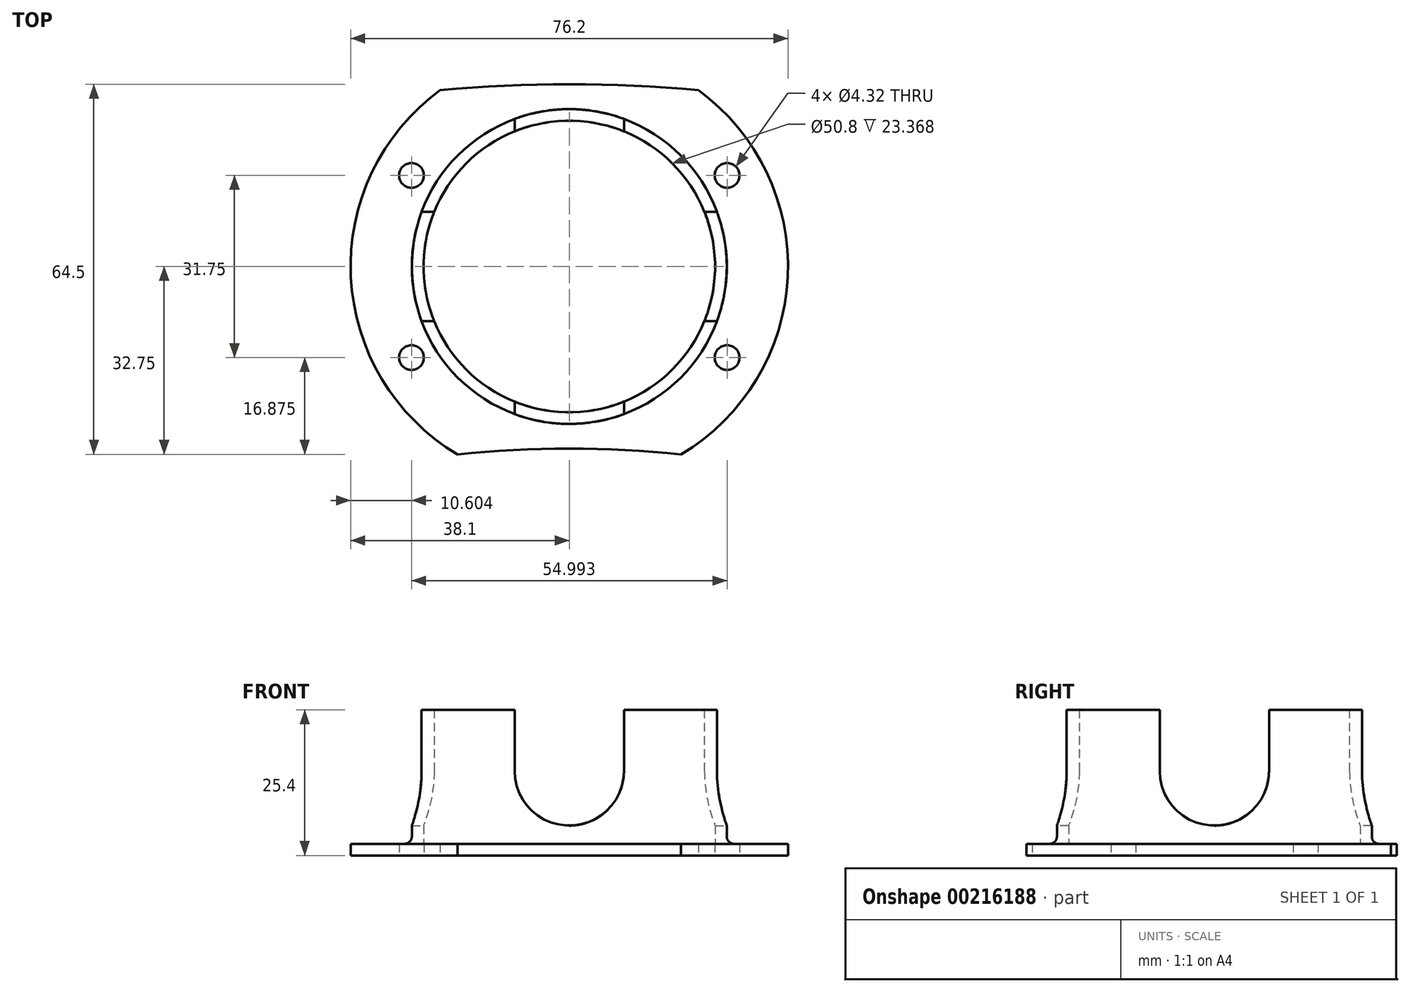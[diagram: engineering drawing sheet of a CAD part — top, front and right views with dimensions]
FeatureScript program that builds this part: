
annotation { "Feature Type Name" : "Feature", "Feature Type Description" : "" }
export const myFeature = defineFeature(function(context is Context, id is Id, definition is map)
    precondition{}
    {
        {
            var Q0;
            Q0=qCreatedBy(makeId("Top.planeOp"),FACE);
            var sketch = newSketch(context, id + "F0", { "sketchPlane" : qUnion([Q0])});
            skCircle(sketch, "E0", {"center": v(0, 0) * mm, "radius": 190.5 * mm});
            skCircle(sketch, "E1", {"center": v(0, 0) * mm, "radius": 254 * mm});
            skLineSegment(sketch, "E2", {"start": v(0, 0) * mm, "end": v(0, 254) * mm});
            skLineSegment(sketch, "E3.1.0", {"start": v(0, 0) * mm, "end": v(-254, 0) * mm});
            skLineSegment(sketch, "E3.2.0", {"start": v(0, 0) * mm, "end": v(0, -254) * mm});
            skLineSegment(sketch, "E3.3.0", {"start": v(0, 0) * mm, "end": v(254, 0) * mm});
            skLineSegment(sketch, "E4", {"start": v(0, 254) * mm, "end": v(0, 190.5) * mm});
            skCircle(sketch, "E5", {"center": v(0, 222.25) * mm, "radius": 31.75 * mm});
            skCircle(sketch, "E6", {"center": v(0, 222.25) * mm, "radius": 25.4 * mm});
            skCircle(sketch, "E7", {"center": v(0, 222.25) * mm, "radius": 38.1 * mm});
            skLineSegment(sketch, "E8", {"start": v(0, 222.25) * mm, "end": v(0, 254) * mm});
            skLineSegment(sketch, "E9.1.0", {"start": v(0, 222.25) * mm, "end": v(-27.5, 238.12) * mm});
            skLineSegment(sketch, "E9.2.0", {"start": v(0, 222.25) * mm, "end": v(-27.5, 206.38) * mm});
            skLineSegment(sketch, "E9.3.0", {"start": v(0, 222.25) * mm, "end": v(0, 190.5) * mm});
            skLineSegment(sketch, "E9.4.0", {"start": v(0, 222.25) * mm, "end": v(27.5, 206.37) * mm});
            skLineSegment(sketch, "E9.5.0", {"start": v(0, 222.25) * mm, "end": v(27.5, 238.12) * mm});
            skCircle(sketch, "E10", {"center": v(0, 222.25) * mm, "radius": 27.43 * mm});
            skSolve(sketch);
        }
        {
            var Q0;
            {var subQ0=sQuery(id+"F0.wireOp",EDGE,"E5");var subQ1=makeQuery(id+"F0.imprint","INTERSECT",VERTEX,{"derivedFrom":[subQ0,sQuery(id+"F0.wireOp",EDGE,"E9.1.0")]});Q0=makeQuery(id+"F0.imprint","IMPRINT",FACE,{"disambiguationData":[TD([[makeQuery(id+"F0.imprint","IMPRINT",EDGE,{"disambiguationData":[TD([[subQ1,-1.0]])],"derivedFrom":subQ0}),-1.0]])]});}
            var Q1;
            {var subQ1=sQuery(id+"F0.wireOp",EDGE,"E5");var subQ3=sQuery(id+"F0.wireOp",EDGE,"E9.1.0");var subQ4=makeQuery(id+"F0.imprint","INTERSECT",VERTEX,{"derivedFrom":[subQ1,subQ3]});Q1=makeQuery(id+"F0.imprint","IMPRINT",FACE,{"disambiguationData":[TD([[makeQuery(id+"F0.imprint","IMPRINT",EDGE,{"disambiguationData":[TD([[subQ4,1.0]])],"derivedFrom":subQ3}),-1.0]])]});}
            var Q2;
            {var subQ0=sQuery(id+"F0.wireOp",EDGE,"E9.1.0");var subQ1=sQuery(id+"F0.wireOp",EDGE,"E5");var subQ2=makeQuery(id+"F0.imprint","INTERSECT",VERTEX,{"derivedFrom":[subQ1,subQ0]});Q2=makeQuery(id+"F0.imprint","IMPRINT",FACE,{"disambiguationData":[TD([[makeQuery(id+"F0.imprint","IMPRINT",EDGE,{"disambiguationData":[TD([[subQ2,-1.0]])],"derivedFrom":subQ1}),1.0]])]});}
            var Q3;
            {var subQ0=sQuery(id+"F0.wireOp",EDGE,"E9.1.0");var subQ1=sQuery(id+"F0.wireOp",EDGE,"E6");var subQ2=makeQuery(id+"F0.imprint","INTERSECT",VERTEX,{"derivedFrom":[subQ1,subQ0]});Q3=makeQuery(id+"F0.imprint","IMPRINT",FACE,{"disambiguationData":[TD([[makeQuery(id+"F0.imprint","IMPRINT",EDGE,{"disambiguationData":[TD([[subQ2,-1.0]])],"derivedFrom":subQ1}),-1.0]])]});}
            var Q4;
            {var subQ1=sQuery(id+"F0.wireOp",EDGE,"E5");var subQ3=sQuery(id+"F0.wireOp",EDGE,"E9.2.0");var subQ4=makeQuery(id+"F0.imprint","INTERSECT",VERTEX,{"derivedFrom":[subQ1,subQ3]});Q4=makeQuery(id+"F0.imprint","IMPRINT",FACE,{"disambiguationData":[TD([[makeQuery(id+"F0.imprint","IMPRINT",EDGE,{"disambiguationData":[TD([[subQ4,1.0]])],"derivedFrom":subQ3}),1.0]])]});}
            var Q5;
            {var subQ0=sQuery(id+"F0.wireOp",EDGE,"E9.2.0");var subQ1=sQuery(id+"F0.wireOp",EDGE,"E6");var subQ2=makeQuery(id+"F0.imprint","INTERSECT",VERTEX,{"derivedFrom":[subQ1,subQ0]});Q5=makeQuery(id+"F0.imprint","IMPRINT",FACE,{"disambiguationData":[TD([[makeQuery(id+"F0.imprint","IMPRINT",EDGE,{"disambiguationData":[TD([[subQ2,-1.0]])],"derivedFrom":subQ1}),-1.0]])]});}
            var Q6;
            {var subQ0=sQuery(id+"F0.wireOp",EDGE,"E9.2.0");var subQ1=sQuery(id+"F0.wireOp",EDGE,"E6");var subQ2=makeQuery(id+"F0.imprint","INTERSECT",VERTEX,{"derivedFrom":[subQ1,subQ0]});Q6=makeQuery(id+"F0.imprint","IMPRINT",FACE,{"disambiguationData":[TD([[makeQuery(id+"F0.imprint","IMPRINT",EDGE,{"disambiguationData":[TD([[subQ2,-1.0]])],"derivedFrom":subQ1}),1.0]])]});}
            var Q7;
            {var subQ0=sQuery(id+"F0.wireOp",EDGE,"E9.1.0");var subQ1=sQuery(id+"F0.wireOp",EDGE,"E6");var subQ2=makeQuery(id+"F0.imprint","INTERSECT",VERTEX,{"derivedFrom":[subQ1,subQ0]});Q7=makeQuery(id+"F0.imprint","IMPRINT",FACE,{"disambiguationData":[TD([[makeQuery(id+"F0.imprint","IMPRINT",EDGE,{"disambiguationData":[TD([[subQ2,-1.0]])],"derivedFrom":subQ1}),1.0]])]});}
            var Q8;
            {var subQ0=sQuery(id+"F0.wireOp",EDGE,"E8");var subQ1=sQuery(id+"F0.wireOp",EDGE,"E6");var subQ2=makeQuery(id+"F0.imprint","INTERSECT",VERTEX,{"derivedFrom":[subQ1,subQ0]});Q8=makeQuery(id+"F0.imprint","IMPRINT",FACE,{"disambiguationData":[TD([[makeQuery(id+"F0.imprint","IMPRINT",EDGE,{"disambiguationData":[TD([[subQ2,-1.0]])],"derivedFrom":subQ1}),1.0]])]});}
            var Q9;
            {var subQ0=sQuery(id+"F0.wireOp",EDGE,"E8");var subQ1=sQuery(id+"F0.wireOp",EDGE,"E6");var subQ2=makeQuery(id+"F0.imprint","INTERSECT",VERTEX,{"derivedFrom":[subQ1,subQ0]});Q9=makeQuery(id+"F0.imprint","IMPRINT",FACE,{"disambiguationData":[TD([[makeQuery(id+"F0.imprint","IMPRINT",EDGE,{"disambiguationData":[TD([[subQ2,-1.0]])],"derivedFrom":subQ1}),-1.0]])]});}
            var Q10;
            {var subQ1=sQuery(id+"F0.wireOp",EDGE,"E5");var subQ3=sQuery(id+"F0.wireOp",EDGE,"E9.5.0");var subQ4=makeQuery(id+"F0.imprint","INTERSECT",VERTEX,{"derivedFrom":[subQ1,subQ3]});Q10=makeQuery(id+"F0.imprint","IMPRINT",FACE,{"disambiguationData":[TD([[makeQuery(id+"F0.imprint","IMPRINT",EDGE,{"disambiguationData":[TD([[subQ4,1.0]])],"derivedFrom":subQ3}),1.0]])]});}
            var Q11;
            {var subQ0=sQuery(id+"F0.wireOp",EDGE,"E8");var subQ1=sQuery(id+"F0.wireOp",EDGE,"E6");var subQ2=makeQuery(id+"F0.imprint","INTERSECT",VERTEX,{"derivedFrom":[subQ1,subQ0]});Q11=makeQuery(id+"F0.imprint","IMPRINT",FACE,{"disambiguationData":[TD([[makeQuery(id+"F0.imprint","IMPRINT",EDGE,{"disambiguationData":[TD([[subQ2,1.0]])],"derivedFrom":subQ1}),-1.0]])]});}
            var Q12;
            {var subQ0=sQuery(id+"F0.wireOp",EDGE,"E8");var subQ1=sQuery(id+"F0.wireOp",EDGE,"E6");var subQ2=makeQuery(id+"F0.imprint","INTERSECT",VERTEX,{"derivedFrom":[subQ1,subQ0]});Q12=makeQuery(id+"F0.imprint","IMPRINT",FACE,{"disambiguationData":[TD([[makeQuery(id+"F0.imprint","IMPRINT",EDGE,{"disambiguationData":[TD([[subQ2,1.0]])],"derivedFrom":subQ1}),1.0]])]});}
            var Q13;
            {var subQ0=sQuery(id+"F0.wireOp",EDGE,"E5");var subQ3=makeQuery(id+"F0.imprint","INTERSECT",VERTEX,{"derivedFrom":[subQ0,sQuery(id+"F0.wireOp",EDGE,"E9.4.0")]});Q13=makeQuery(id+"F0.imprint","IMPRINT",FACE,{"disambiguationData":[TD([[makeQuery(id+"F0.imprint","IMPRINT",EDGE,{"disambiguationData":[TD([[subQ3,-1.0]])],"derivedFrom":subQ0}),-1.0]])]});}
            var Q14;
            {var subQ0=sQuery(id+"F0.wireOp",EDGE,"E9.4.0");var subQ1=sQuery(id+"F0.wireOp",EDGE,"E5");var subQ2=makeQuery(id+"F0.imprint","INTERSECT",VERTEX,{"derivedFrom":[subQ1,subQ0]});Q14=makeQuery(id+"F0.imprint","IMPRINT",FACE,{"disambiguationData":[TD([[makeQuery(id+"F0.imprint","IMPRINT",EDGE,{"disambiguationData":[TD([[subQ2,-1.0]])],"derivedFrom":subQ1}),1.0]])]});}
            var Q15;
            {var subQ0=sQuery(id+"F0.wireOp",EDGE,"E9.5.0");var subQ1=sQuery(id+"F0.wireOp",EDGE,"E6");var subQ2=makeQuery(id+"F0.imprint","INTERSECT",VERTEX,{"derivedFrom":[subQ1,subQ0]});Q15=makeQuery(id+"F0.imprint","IMPRINT",FACE,{"disambiguationData":[TD([[makeQuery(id+"F0.imprint","IMPRINT",EDGE,{"disambiguationData":[TD([[subQ2,1.0]])],"derivedFrom":subQ1}),-1.0]])]});}
            var Q16;
            {var subQ0=sQuery(id+"F0.wireOp",EDGE,"E9.5.0");var subQ1=sQuery(id+"F0.wireOp",EDGE,"E6");var subQ2=makeQuery(id+"F0.imprint","INTERSECT",VERTEX,{"derivedFrom":[subQ1,subQ0]});Q16=makeQuery(id+"F0.imprint","IMPRINT",FACE,{"disambiguationData":[TD([[makeQuery(id+"F0.imprint","IMPRINT",EDGE,{"disambiguationData":[TD([[subQ2,1.0]])],"derivedFrom":subQ1}),1.0]])]});}
            var Q17;
            {var subQ0=sQuery(id+"F0.wireOp",EDGE,"E9.3.0");var subQ1=sQuery(id+"F0.wireOp",EDGE,"E6");var subQ2=makeQuery(id+"F0.imprint","INTERSECT",VERTEX,{"derivedFrom":[subQ1,subQ0]});Q17=makeQuery(id+"F0.imprint","IMPRINT",FACE,{"disambiguationData":[TD([[makeQuery(id+"F0.imprint","IMPRINT",EDGE,{"disambiguationData":[TD([[subQ2,-1.0]])],"derivedFrom":subQ1}),1.0]])]});}
            var Q18;
            {var subQ0=sQuery(id+"F0.wireOp",EDGE,"E9.3.0");var subQ1=sQuery(id+"F0.wireOp",EDGE,"E6");var subQ2=makeQuery(id+"F0.imprint","INTERSECT",VERTEX,{"derivedFrom":[subQ1,subQ0]});Q18=makeQuery(id+"F0.imprint","IMPRINT",FACE,{"disambiguationData":[TD([[makeQuery(id+"F0.imprint","IMPRINT",EDGE,{"disambiguationData":[TD([[subQ2,-1.0]])],"derivedFrom":subQ1}),-1.0]])]});}
            var Q19;
            {var subQ1=sQuery(id+"F0.wireOp",EDGE,"E5");var subQ3=sQuery(id+"F0.wireOp",EDGE,"E9.4.0");var subQ4=makeQuery(id+"F0.imprint","INTERSECT",VERTEX,{"derivedFrom":[subQ1,subQ3]});Q19=makeQuery(id+"F0.imprint","IMPRINT",FACE,{"disambiguationData":[TD([[makeQuery(id+"F0.imprint","IMPRINT",EDGE,{"disambiguationData":[TD([[subQ4,1.0]])],"derivedFrom":subQ3}),-1.0]])]});}
            extrude(context, id + "F1", {"entities" : qUnion([Q0, Q1, Q2, Q3, Q4, Q5, Q6, Q7, Q8, Q9, Q10, Q11, Q12, Q13, Q14, Q15, Q16, Q17, Q18, Q19]), "depth" : 2.03 * mm});
        }
        {
            var Q0;
            {var subQ0=sQuery(id+"F0.wireOp",EDGE,"E9.2.0");var subQ1=sQuery(id+"F0.wireOp",EDGE,"E6");var subQ2=makeQuery(id+"F0.imprint","INTERSECT",VERTEX,{"derivedFrom":[subQ1,subQ0]});Q0=makeQuery(id+"F0.imprint","IMPRINT",FACE,{"disambiguationData":[TD([[makeQuery(id+"F0.imprint","IMPRINT",EDGE,{"disambiguationData":[TD([[subQ2,-1.0]])],"derivedFrom":subQ1}),-1.0]])]});}
            var Q1;
            {var subQ0=sQuery(id+"F0.wireOp",EDGE,"E9.1.0");var subQ1=sQuery(id+"F0.wireOp",EDGE,"E6");var subQ2=makeQuery(id+"F0.imprint","INTERSECT",VERTEX,{"derivedFrom":[subQ1,subQ0]});Q1=makeQuery(id+"F0.imprint","IMPRINT",FACE,{"disambiguationData":[TD([[makeQuery(id+"F0.imprint","IMPRINT",EDGE,{"disambiguationData":[TD([[subQ2,-1.0]])],"derivedFrom":subQ1}),-1.0]])]});}
            var Q2;
            {var subQ0=sQuery(id+"F0.wireOp",EDGE,"E8");var subQ1=sQuery(id+"F0.wireOp",EDGE,"E6");var subQ2=makeQuery(id+"F0.imprint","INTERSECT",VERTEX,{"derivedFrom":[subQ1,subQ0]});Q2=makeQuery(id+"F0.imprint","IMPRINT",FACE,{"disambiguationData":[TD([[makeQuery(id+"F0.imprint","IMPRINT",EDGE,{"disambiguationData":[TD([[subQ2,-1.0]])],"derivedFrom":subQ1}),-1.0]])]});}
            var Q3;
            {var subQ0=sQuery(id+"F0.wireOp",EDGE,"E8");var subQ1=sQuery(id+"F0.wireOp",EDGE,"E6");var subQ2=makeQuery(id+"F0.imprint","INTERSECT",VERTEX,{"derivedFrom":[subQ1,subQ0]});Q3=makeQuery(id+"F0.imprint","IMPRINT",FACE,{"disambiguationData":[TD([[makeQuery(id+"F0.imprint","IMPRINT",EDGE,{"disambiguationData":[TD([[subQ2,1.0]])],"derivedFrom":subQ1}),-1.0]])]});}
            var Q4;
            {var subQ0=sQuery(id+"F0.wireOp",EDGE,"E9.5.0");var subQ1=sQuery(id+"F0.wireOp",EDGE,"E6");var subQ2=makeQuery(id+"F0.imprint","INTERSECT",VERTEX,{"derivedFrom":[subQ1,subQ0]});Q4=makeQuery(id+"F0.imprint","IMPRINT",FACE,{"disambiguationData":[TD([[makeQuery(id+"F0.imprint","IMPRINT",EDGE,{"disambiguationData":[TD([[subQ2,1.0]])],"derivedFrom":subQ1}),-1.0]])]});}
            var Q5;
            {var subQ0=sQuery(id+"F0.wireOp",EDGE,"E9.3.0");var subQ1=sQuery(id+"F0.wireOp",EDGE,"E6");var subQ2=makeQuery(id+"F0.imprint","INTERSECT",VERTEX,{"derivedFrom":[subQ1,subQ0]});Q5=makeQuery(id+"F0.imprint","IMPRINT",FACE,{"disambiguationData":[TD([[makeQuery(id+"F0.imprint","IMPRINT",EDGE,{"disambiguationData":[TD([[subQ2,-1.0]])],"derivedFrom":subQ1}),-1.0]])]});}
            extrude(context, id + "F2", {"entities" : qUnion([Q0, Q1, Q2, Q3, Q4, Q5]), "operationType" : NewBodyOperationType.ADD, "depth" : 25.4 * mm});
        }
        {
            var Q0;
            Q0=sQuery(id+"F0.wireOp",VERTEX,"E9.2.0.end");
            var Q1;
            Q1=sQuery(id+"F0.wireOp",VERTEX,"E9.1.0.end");
            var Q2;
            Q2=sQuery(id+"F0.wireOp",VERTEX,"E9.5.0.end");
            var Q3;
            Q3=sQuery(id+"F0.wireOp",VERTEX,"E9.4.0.end");
            var Q4;
            Q4=makeQuery(id+"F1.opExtrude","SWEPT_BODY",BODY,{"disambiguationData":[OSD([sQuery(id+"F0.wireOp",EDGE,"E0"),sQuery(id+"F0.wireOp",EDGE,"E1"),sQuery(id+"F0.wireOp",EDGE,"E7")])]});
            hole(context, id + "F3", {"style" : HoleStyle.SIMPLE, "endStyle" : HoleEndStyle.BLIND, "oppositeDirection" : true, "standardTappedOrClearance" : lookupTablePath({ "standard" : "ANSI", "fit" : "Close", "size" : "#8", "type" : "Clearance" }), "standardBlindInLast" : lookupTablePath({ "fit" : "Close", "standard" : "ANSI", "size" : "#8", "type" : "Clearance" }), "holeDiameter" : 4.32 * mm, "holeDepth" : 5.08 * mm, "locations" : qUnion([Q0, Q1, Q2, Q3]), "scope" : qUnion([Q4])});
        }
        {
            var Q0;
            Q0=sQuery(id+"F0.wireOp",EDGE,"E8");
            cPlane(context, id + "F4", {"entities" : qUnion([Q0]), "cplaneType" : CPlaneType.LINE_ANGLE, "offset" : 25.4 * mm, "angle" : 90 * degree, "width" : 152.4 * mm, "height" : 152.4 * mm});
        }
        {
            var Q0;
            Q0=qCreatedBy(id+"F4.planeOp",FACE);
            var sketch = newSketch(context, id + "F5", { "sketchPlane" : qUnion([Q0])});
            skLineSegment(sketch, "E11", {"start": v(222.25, 0) * mm, "end": v(222.25, 14.73) * mm});
            skArc(sketch, "E12", {"start": v(212.72, 14.73) * mm, "mid": v(222.25, 5.2) * mm, "end": v(231.78, 14.73) * mm});
            skLineSegment(sketch, "E13", {"start": v(231.78, 14.73) * mm, "end": v(231.78, 28.62) * mm});
            skLineSegment(sketch, "E14", {"start": v(231.78, 28.62) * mm, "end": v(212.72, 28.62) * mm});
            skLineSegment(sketch, "E15", {"start": v(212.72, 28.62) * mm, "end": v(212.72, 14.73) * mm});
            skSolve(sketch);
        }
        {
            var Q0;
            Q0 = qSketchRegion(id + "F5", true);
            extrude(context, id + "F6", {"entities" : qUnion([Q0]), "operationType" : NewBodyOperationType.REMOVE, "endBound" : BoundingType.SYMMETRIC, "oppositeDirection" : true, "depth" : 127 * mm});
        }
        {
            var Q0;
            {var subQ0=sQuery(id+"F0.wireOp",EDGE,"E7");var subQ1=sQuery(id+"F0.wireOp",EDGE,"E1");var subQ2=sQuery(id+"F0.wireOp",EDGE,"E0");Q0=makeQuery(id+"F2.boolean.opBoolean","SPLIT",FACE,{"disambiguationData":[TD([makeQuery(id+"F1.opExtrude","SWEPT_FACE",FACE,{"disambiguationData":[OSD([subQ2])]})])],"derivedFrom":makeQuery(id+"F1.opExtrude","CAP_FACE",FACE,{"disambiguationData":[OSD([subQ2,subQ1,subQ0])],"isStart":false})});}
            var sketch = newSketch(context, id + "F7", { "sketchPlane" : qUnion([Q0])});
            skLineSegment(sketch, "E16", {"start": v(0, 222.25) * mm, "end": v(-18.46, 222.25) * mm});
            skSolve(sketch);
        }
        {
            var Q0;
            Q0=sQuery(id+"F7.wireOp",EDGE,"E16");
            cPlane(context, id + "F8", {"entities" : qUnion([Q0]), "cplaneType" : CPlaneType.LINE_ANGLE, "offset" : 25.4 * mm, "angle" : 0 * degree, "width" : 152.4 * mm, "height" : 152.4 * mm});
        }
        {
            var Q0;
            Q0=qCreatedBy(id+"F8.planeOp",FACE);
            var sketch = newSketch(context, id + "F9", { "sketchPlane" : qUnion([Q0])});
            skLineSegment(sketch, "E17", {"start": v(0, 0) * mm, "end": v(0, 14.73) * mm});
            skArc(sketch, "E18", {"start": v(-9.53, 14.73) * mm, "mid": v(0, 5.2) * mm, "end": v(9.53, 14.73) * mm});
            skLineSegment(sketch, "E19", {"start": v(9.53, 14.73) * mm, "end": v(9.53, 30.18) * mm});
            skLineSegment(sketch, "E20", {"start": v(9.53, 30.18) * mm, "end": v(-9.53, 30.18) * mm});
            skLineSegment(sketch, "E21", {"start": v(-9.53, 30.18) * mm, "end": v(-9.53, 14.73) * mm});
            skSolve(sketch);
        }
        {
            var Q0;
            Q0 = qSketchRegion(id + "F9", true);
            extrude(context, id + "F10", {"entities" : qUnion([Q0]), "operationType" : NewBodyOperationType.REMOVE, "endBound" : BoundingType.SYMMETRIC, "oppositeDirection" : true, "depth" : 127 * mm});
        }
        {
            var Q0;
            Q0=makeQuery(id+"F2.boolean.opBoolean","INTERSECT",EDGE,{"derivedFrom":[makeQuery(id+"F1.opExtrude","CAP_FACE",FACE,{"disambiguationData":[OSD([sQuery(id+"F0.wireOp",EDGE,"E0"),sQuery(id+"F0.wireOp",EDGE,"E1"),sQuery(id+"F0.wireOp",EDGE,"E7")])],"isStart":false}),makeQuery(id+"F2.opExtrude","SWEPT_FACE",FACE,{"disambiguationData":[OSD([sQuery(id+"F0.wireOp",EDGE,"E10")])]})]});
            fillet(context, id + "F11", {"entities" : qUnion([Q0]), "radius" : 1.27 * mm, "tangentPropagation" : true, "allowEdgeOverflow" : false});
        }
    });
